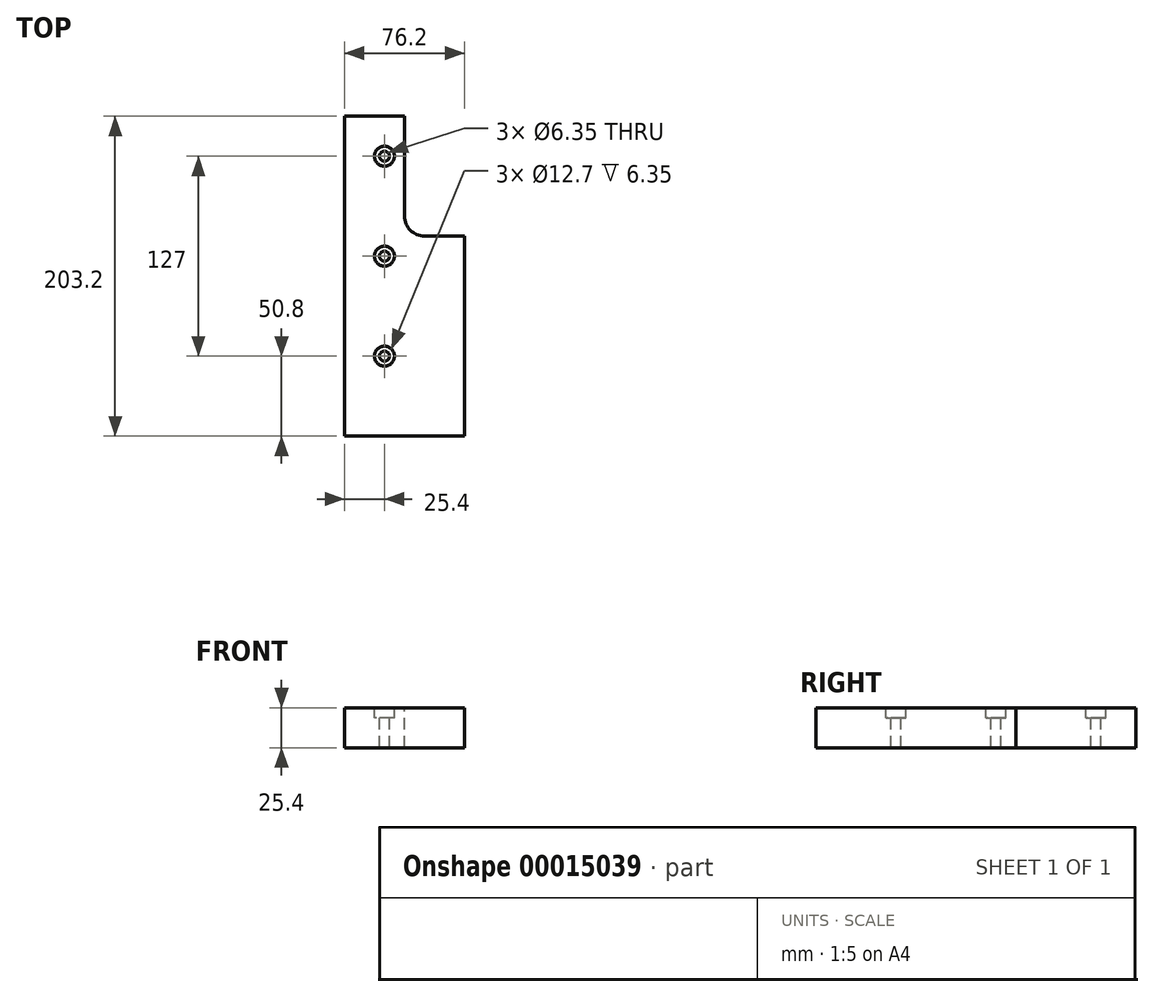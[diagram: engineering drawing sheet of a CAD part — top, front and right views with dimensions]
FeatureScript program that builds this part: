
annotation { "Feature Type Name" : "Feature", "Feature Type Description" : "" }
export const myFeature = defineFeature(function(context is Context, id is Id, definition is map)
    precondition{}
    {
        {
            var Q0;
            Q0=qCreatedBy(makeId("Top.planeOp"),FACE);
            var sketch = newSketch(context, id + "F0", { "sketchPlane" : qUnion([Q0])});
            skLineSegment(sketch, "E0.bottom", {"start": v(-76.2, 0) * mm, "end": v(0, 0) * mm});
            skLineSegment(sketch, "E0.top", {"start": v(-76.2, 203.2) * mm, "end": v(0, 203.2) * mm});
            skLineSegment(sketch, "E0.left", {"start": v(-76.2, 0) * mm, "end": v(-76.2, 203.2) * mm});
            skLineSegment(sketch, "E0.right", {"start": v(0, 0) * mm, "end": v(0, 203.2) * mm});
            skSolve(sketch);
        }
        {
            var Q0;
            Q0 = qSketchRegion(id + "F0", true);
            extrude(context, id + "F1", {"entities" : qUnion([Q0]), "endBound" : BoundingType.SYMMETRIC, "depth" : 25.4 * mm});
        }
        {
            var Q0;
            Q0=makeQuery(id+"F1.opExtrude","CAP_FACE",FACE,{"disambiguationData":[OSD([sQuery(id+"F0.wireOp",EDGE,"E0.bottom"),sQuery(id+"F0.wireOp",EDGE,"E0.top"),sQuery(id+"F0.wireOp",EDGE,"E0.left"),sQuery(id+"F0.wireOp",EDGE,"E0.right")])],"isStart":false});
            var sketch = newSketch(context, id + "F2", { "sketchPlane" : qUnion([Q0])});
            skPoint(sketch, "E1", {"position": v(-50.8, 177.8) * mm});
            skPoint(sketch, "E2", {"position": v(-50.8, 114.3) * mm});
            skPoint(sketch, "E3", {"position": v(-50.8, 50.8) * mm});
            skLineSegment(sketch, "E4", {"start": v(-50.8, 177.8) * mm, "end": v(-50.8, 114.3) * mm, "construction": true});
            skLineSegment(sketch, "E5", {"start": v(-50.8, 114.3) * mm, "end": v(-50.8, 50.8) * mm, "construction": true});
            skSolve(sketch);
        }
        {
            var Q0;
            Q0=sQuery(id+"F2.wireOp",VERTEX,"E3");
            var Q1;
            Q1=sQuery(id+"F2.wireOp",VERTEX,"E2");
            var Q2;
            Q2=sQuery(id+"F2.wireOp",VERTEX,"E1");
            var Q3;
            Q3=makeQuery(id+"F1.opExtrude","SWEPT_BODY",BODY,{"disambiguationData":[OSD([sQuery(id+"F0.wireOp",EDGE,"E0.bottom"),sQuery(id+"F0.wireOp",EDGE,"E0.top"),sQuery(id+"F0.wireOp",EDGE,"E0.left"),sQuery(id+"F0.wireOp",EDGE,"E0.right")])]});
            hole(context, id + "F3", {"style" : HoleStyle.C_BORE, "holeDiameter" : 6.35 * mm, "cBoreDiameter" : 12.7 * mm, "cBoreDepth" : 6.35 * mm, "endStyle" : HoleEndStyle.THROUGH, "locations" : qUnion([Q0, Q1, Q2]), "scope" : qUnion([Q3])});
        }
        {
            var Q0;
            Q0=makeQuery(id+"F1.opExtrude","CAP_FACE",FACE,{"disambiguationData":[OSD([sQuery(id+"F0.wireOp",EDGE,"E0.bottom"),sQuery(id+"F0.wireOp",EDGE,"E0.top"),sQuery(id+"F0.wireOp",EDGE,"E0.left"),sQuery(id+"F0.wireOp",EDGE,"E0.right")])],"isStart":false});
            var sketch = newSketch(context, id + "F4", { "sketchPlane" : qUnion([Q0])});
            skLineSegment(sketch, "E6.bottom", {"start": v(-38.1, 203.2) * mm, "end": v(0, 203.2) * mm});
            skLineSegment(sketch, "E6.top", {"start": v(-38.1, 127) * mm, "end": v(0, 127) * mm});
            skLineSegment(sketch, "E6.left", {"start": v(-38.1, 203.2) * mm, "end": v(-38.1, 127) * mm});
            skLineSegment(sketch, "E6.right", {"start": v(0, 203.2) * mm, "end": v(0, 127) * mm});
            skSolve(sketch);
        }
        {
            var Q0;
            Q0 = qSketchRegion(id + "F4", true);
            extrude(context, id + "F5", {"entities" : qUnion([Q0]), "operationType" : NewBodyOperationType.REMOVE, "endBound" : BoundingType.UP_TO_NEXT, "oppositeDirection" : true, "depth" : 25.4 * mm});
        }
        {
            var Q0;
            Q0=makeQuery(id+"F5.boolean.opBoolean","COPY",EDGE,{"derivedFrom":makeQuery(id+"F5.opExtrude","SWEPT_EDGE",EDGE,{"disambiguationData":[OSD([sQuery(id+"F4.wireOp",EDGE,"E6.top"),sQuery(id+"F4.wireOp",EDGE,"E6.left")])]})});
            fillet(context, id + "F6", {"entities" : qUnion([Q0]), "radius" : 12.7 * mm, "tangentPropagation" : true, "allowEdgeOverflow" : false});
        }
    });
